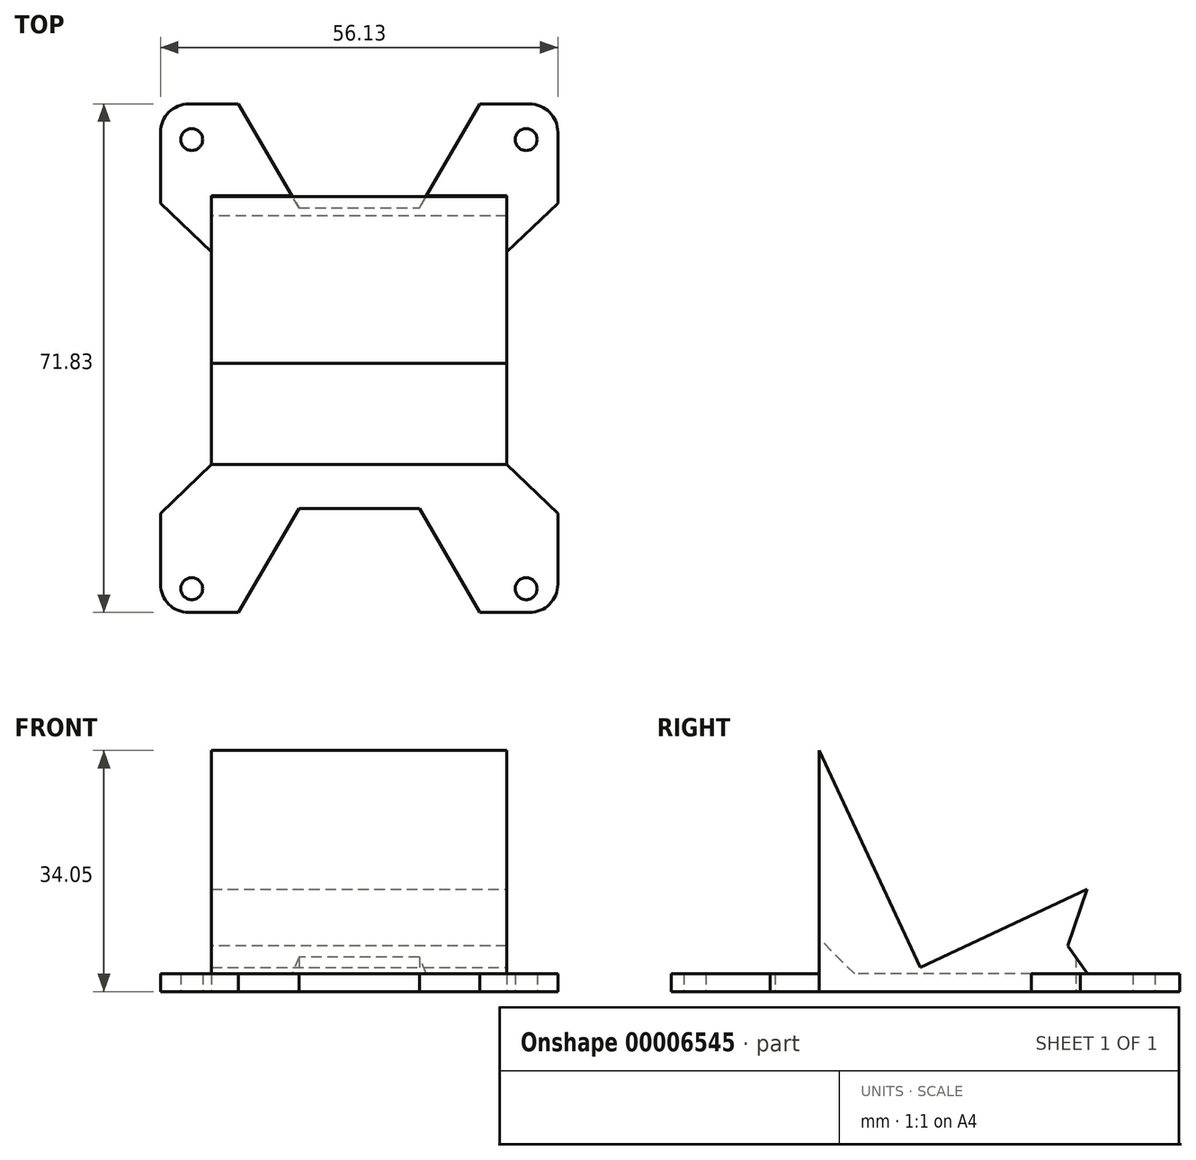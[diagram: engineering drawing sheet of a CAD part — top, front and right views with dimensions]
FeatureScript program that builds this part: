
annotation { "Feature Type Name" : "Feature", "Feature Type Description" : "" }
export const myFeature = defineFeature(function(context is Context, id is Id, definition is map)
    precondition{}
    {
        {
            var Q0;
            Q0=qCreatedBy(makeId("Top.planeOp"),FACE);
            var sketch = newSketch(context, id + "F0", { "sketchPlane" : qUnion([Q0])});
            skLineSegment(sketch, "E0.bottom", {"start": v(4, 71.83) * mm, "end": v(52.13, 71.83) * mm});
            skLineSegment(sketch, "E0.top", {"start": v(4, 0) * mm, "end": v(52.13, 0) * mm});
            skLineSegment(sketch, "E0.left", {"start": v(0, 67.83) * mm, "end": v(0, 4) * mm});
            skLineSegment(sketch, "E0.right", {"start": v(56.13, 67.83) * mm, "end": v(56.13, 4) * mm});
            skCircle(sketch, "E1", {"center": v(4.42, 66.81) * mm, "radius": 1.55 * mm});
            skCircle(sketch, "E2", {"center": v(4.42, 3.37) * mm, "radius": 1.55 * mm});
            skPoint(sketch, "E3.visualSharp", {"position": v(0, 71.83) * mm});
            skArc(sketch, "E3.filletArc", {"start": v(4, 71.83) * mm, "mid": v(1.17, 70.66) * mm, "end": v(0, 67.83) * mm});
            skCircle(sketch, "E4", {"center": v(51.65, 66.81) * mm, "radius": 1.55 * mm});
            skCircle(sketch, "E5", {"center": v(51.65, 3.37) * mm, "radius": 1.55 * mm});
            skPoint(sketch, "E6.visualSharp", {"position": v(56.13, 71.83) * mm});
            skArc(sketch, "E6.filletArc", {"start": v(56.13, 67.83) * mm, "mid": v(54.95, 70.66) * mm, "end": v(52.13, 71.83) * mm});
            skPoint(sketch, "E7.visualSharp", {"position": v(56.13, 0) * mm});
            skArc(sketch, "E7.filletArc", {"start": v(52.13, 0) * mm, "mid": v(54.95, 1.17) * mm, "end": v(56.13, 4) * mm});
            skPoint(sketch, "E8.visualSharp", {"position": v(0, 0) * mm});
            skArc(sketch, "E8.filletArc", {"start": v(0, 4) * mm, "mid": v(1.17, 1.17) * mm, "end": v(4, 0) * mm});
            skLineSegment(sketch, "E9", {"start": v(11, 71.83) * mm, "end": v(19.56, 57.15) * mm});
            skLineSegment(sketch, "E10", {"start": v(19.56, 57.15) * mm, "end": v(36.56, 57.15) * mm});
            skLineSegment(sketch, "E11", {"start": v(36.56, 57.15) * mm, "end": v(45.13, 71.83) * mm});
            skLineSegment(sketch, "E12", {"start": v(0, 57.83) * mm, "end": v(7.22, 50.92) * mm});
            skLineSegment(sketch, "E13", {"start": v(7.22, 50.92) * mm, "end": v(7.22, 20.92) * mm});
            skLineSegment(sketch, "E14", {"start": v(7.22, 20.92) * mm, "end": v(0, 14) * mm});
            skLineSegment(sketch, "E15", {"start": v(56.13, 57.83) * mm, "end": v(48.9, 50.92) * mm});
            skLineSegment(sketch, "E16", {"start": v(48.9, 50.92) * mm, "end": v(48.9, 20.92) * mm});
            skLineSegment(sketch, "E17", {"start": v(48.9, 20.92) * mm, "end": v(56.13, 14) * mm});
            skLineSegment(sketch, "E18", {"start": v(11, 0) * mm, "end": v(19.56, 14.69) * mm});
            skLineSegment(sketch, "E19", {"start": v(19.56, 14.69) * mm, "end": v(36.56, 14.69) * mm});
            skLineSegment(sketch, "E20", {"start": v(36.56, 14.69) * mm, "end": v(45.13, 0) * mm});
            skSolve(sketch);
        }
        {
            var Q0;
            Q0=makeQuery(id+"F0.imprint","IMPRINT",FACE,{"disambiguationData":[TD([[makeQuery(id+"F0.imprint","IMPRINT",EDGE,{"derivedFrom":sQuery(id+"F0.wireOp",EDGE,"E1")}),-1.0]])]});
            extrude(context, id + "F1", {"entities" : qUnion([Q0]), "depth" : 2.5 * mm});
        }
        {
            var Q0;
            Q0=makeQuery(id+"F1.opExtrude","SWEPT_FACE",FACE,{"disambiguationData":[OSD([sQuery(id+"F0.wireOp",EDGE,"E16")])]});
            var sketch = newSketch(context, id + "F2", { "sketchPlane" : qUnion([Q0])});
            skLineSegment(sketch, "E21", {"start": v(20.92, 2.5) * mm, "end": v(20.92, 34.05) * mm});
            skLineSegment(sketch, "E22", {"start": v(20.92, 34.05) * mm, "end": v(35.2, 3.44) * mm});
            skLineSegment(sketch, "E23", {"start": v(35.2, 3.44) * mm, "end": v(58.76, 14.42) * mm});
            skLineSegment(sketch, "E24", {"start": v(50.92, 2.5) * mm, "end": v(54.65, 2.5) * mm});
            skLineSegment(sketch, "E25", {"start": v(54.65, 2.5) * mm, "end": v(58.76, 14.42) * mm});
            skSolve(sketch);
        }
        {
            var Q0;
            Q0 = qSketchRegion(id + "F2", true);
            var Q1;
            Q1=makeQuery(id+"F2.imprint","IMPRINT",FACE,{"disambiguationData":[TD([[makeQuery(id+"F2.imprint","IMPRINT",EDGE,{"derivedFrom":sQuery(id+"F2.wireOp",EDGE,"E21")}),-1.0]])]});
            extrude(context, id + "F3", {"entities" : qUnion([Q0, Q1]), "operationType" : NewBodyOperationType.ADD, "oppositeDirection" : true, "depth" : 41.7 * mm});
        }
        {
            var Q0;
            {var subQ0=sQuery(id+"F0.wireOp",EDGE,"E16");var subQ1=sQuery(id+"F0.wireOp",EDGE,"E17");var subQ2=sQuery(id+"F2.wireOp",EDGE,"E21");Q0=makeQuery(id+"F3.boolean.opBoolean","SPLIT",EDGE,{"disambiguationData":[TD([makeQuery(id+"F1.opExtrude","SWEPT_FACE",FACE,{"disambiguationData":[OSD([subQ0])]})])],"derivedFrom":makeQuery(id+"F3.opExtrude","SWEPT_EDGE",EDGE,{"disambiguationData":[OSD([subQ0,subQ1,subQ2])]})});}
            chamfer(context, id + "F4", {"entities" : qUnion([Q0]), "width" : 5 * mm, "tangentPropagation" : true});
        }
        {
            var Q0;
            Q0=makeQuery(id+"F3.opExtrude","SWEPT_EDGE",EDGE,{"disambiguationData":[OSD([sQuery(id+"F2.wireOp",EDGE,"E24"),sQuery(id+"F2.wireOp",EDGE,"E25")])]});
            chamfer(context, id + "F5", {"entities" : qUnion([Q0]), "width" : 3 * mm, "tangentPropagation" : true});
        }
    });
